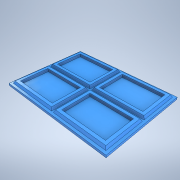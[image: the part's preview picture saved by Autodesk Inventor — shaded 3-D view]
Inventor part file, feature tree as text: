
AUTODESK INVENTOR PART (.ipt)
format: ipt  version: 2021 (Build 250183000, 183)  size: 214,528 bytes
history: native  units: mm
features: extrude x6, sketch x6
ambient origin geometry x8: Origin, YZ Plane, XZ Plane, XY Plane, X Axis, Y Axis, Z Axis, Center Point
bodies: Body1 (feature_tree)
feature tree (12):
  extrude  "Extrusion9"  Depth=105.0mm
  extrude  "Extrusion10"  Depth=6.0mm
  extrude  "Extrusion11"  Depth=140.0mm
  extrude  "Extrusion12"  Depth=3.0mm TaperAngle=0.0deg
  extrude  "Extrusion15"  Depth=5.0mm TaperAngle=0.0deg
  extrude  "Extrusion16"  Depth=5.0mm
  sketch  "Sketch16"  dims[d141=140.0mm d142=105.0mm]
  sketch  "Sketch17"  dims[d143=3.0mm d144=0.0mm]
  sketch  "Sketch18"  dims[d146=20.0mm d148=20.0mm d149=140.0mm d150=105.0mm d151=44.5mm d152=62.0mm d153=5.0mm d154=5.0mm d155=68.0mm d156=50.5mm d157=6.0mm d158=-5.235988mm]
  sketch  "Sketch19"  dims[d159=0.0mm d160=0.0mm d161=140.0mm]
  sketch  "Sketch22"  dims[d162=105.0mm d163=3.0mm d164=0.0mm]
  sketch  "Sketch24"  dims[d205=2.0mm d206=0.0mm d207=6.0mm d208=20.0mm d210=50.5mm d211=20.0mm d213=68.0mm d216=5.0mm d217=0.0mm d82=0.5mm d83=0.872665mm d84=0.5mm d85=0.872665mm d86=0.5mm d87=0.872665mm]
